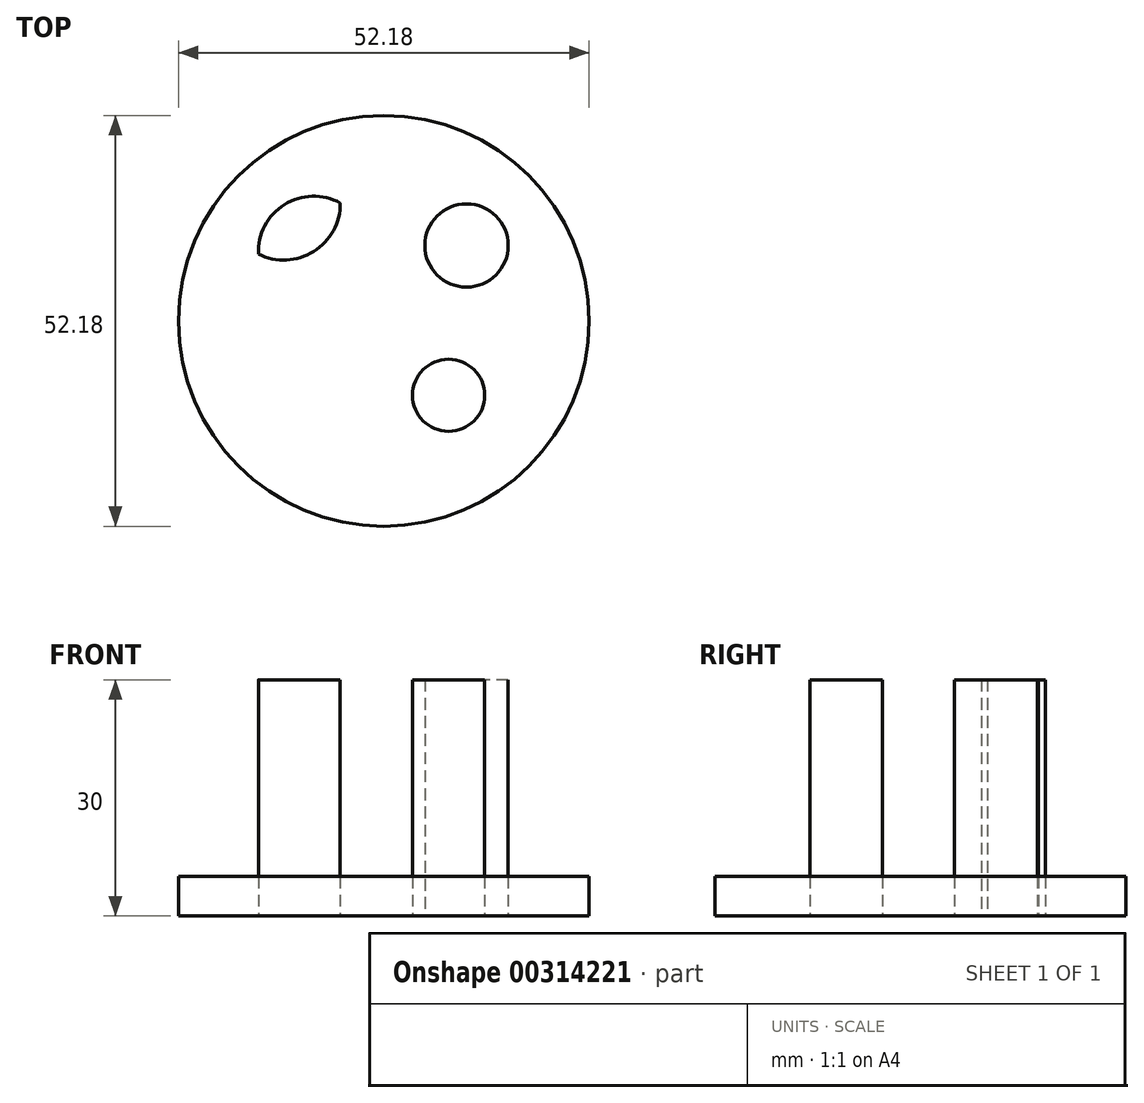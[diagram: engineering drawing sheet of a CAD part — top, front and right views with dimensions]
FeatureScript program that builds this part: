
annotation { "Feature Type Name" : "Feature", "Feature Type Description" : "" }
export const myFeature = defineFeature(function(context is Context, id is Id, definition is map)
    precondition{}
    {
        {
            var Q0;
            Q0=qCreatedBy(makeId("Top.planeOp"),FACE);
            var sketch = newSketch(context, id + "F0", { "sketchPlane" : qUnion([Q0])});
            skCircle(sketch, "E0", {"center": v(0, 0) * mm, "radius": 26.1 * mm});
            skCircle(sketch, "E1", {"center": v(10.52, 9.59) * mm, "radius": 5.29 * mm});
            skCircle(sketch, "E2", {"center": v(8.23, -9.44) * mm, "radius": 4.58 * mm});
            skCircle(sketch, "E3", {"center": v(-12.7, 14.92) * mm, "radius": 7.18 * mm});
            skCircle(sketch, "E4", {"center": v(-8.9, 8.83) * mm, "radius": 7.02 * mm});
            skSolve(sketch);
        }
        {
            var Q0;
            Q0=makeQuery(id+"F0.imprint","IMPRINT",FACE,{"disambiguationData":[TD([[makeQuery(id+"F0.imprint","IMPRINT",EDGE,{"derivedFrom":sQuery(id+"F0.wireOp",EDGE,"E1")}),1.0]])]});
            var Q1;
            Q1=makeQuery(id+"F0.imprint","IMPRINT",FACE,{"disambiguationData":[TD([[makeQuery(id+"F0.imprint","IMPRINT",EDGE,{"derivedFrom":sQuery(id+"F0.wireOp",EDGE,"E2")}),1.0]])]});
            var Q2;
            {var subQ0=sQuery(id+"F0.wireOp",EDGE,"E4");var subQ1=sQuery(id+"F0.wireOp",EDGE,"E3");var subQ2=makeQuery(id+"F0.imprint","INTERSECT",VERTEX,{"disambiguationData":[OD(0.0)],"derivedFrom":[subQ1,subQ0]});Q2=makeQuery(id+"F0.imprint","IMPRINT",FACE,{"disambiguationData":[TD([[makeQuery(id+"F0.imprint","IMPRINT",EDGE,{"disambiguationData":[TD([[subQ2,1.0]])],"derivedFrom":subQ1}),1.0]])]});}
            extrude(context, id + "F1", {"entities" : qUnion([Q0, Q1, Q2]), "depth" : 30 * mm});
        }
        {
            var Q0;
            Q0=makeQuery(id+"F0.imprint","IMPRINT",FACE,{"disambiguationData":[TD([[makeQuery(id+"F0.imprint","IMPRINT",EDGE,{"derivedFrom":sQuery(id+"F0.wireOp",EDGE,"E1")}),-1.0]])]});
            var Q1;
            Q1=makeQuery(id+"F0.imprint","IMPRINT",FACE,{"disambiguationData":[TD([[makeQuery(id+"F0.imprint","IMPRINT",EDGE,{"derivedFrom":sQuery(id+"F0.wireOp",EDGE,"E2")}),1.0]])]});
            var Q2;
            Q2=makeQuery(id+"F0.imprint","IMPRINT",FACE,{"disambiguationData":[TD([[makeQuery(id+"F0.imprint","IMPRINT",EDGE,{"derivedFrom":sQuery(id+"F0.wireOp",EDGE,"E1")}),1.0]])]});
            var Q3;
            {var subQ0=sQuery(id+"F0.wireOp",EDGE,"E4");var subQ1=sQuery(id+"F0.wireOp",EDGE,"E3");var subQ2=makeQuery(id+"F0.imprint","INTERSECT",VERTEX,{"disambiguationData":[OD(0.0)],"derivedFrom":[subQ1,subQ0]});Q3=makeQuery(id+"F0.imprint","IMPRINT",FACE,{"disambiguationData":[TD([[makeQuery(id+"F0.imprint","IMPRINT",EDGE,{"disambiguationData":[TD([[subQ2,1.0]])],"derivedFrom":subQ1}),-1.0]])]});}
            var Q4;
            {var subQ0=sQuery(id+"F0.wireOp",EDGE,"E4");var subQ1=sQuery(id+"F0.wireOp",EDGE,"E3");var subQ2=makeQuery(id+"F0.imprint","INTERSECT",VERTEX,{"disambiguationData":[OD(0.0)],"derivedFrom":[subQ1,subQ0]});Q4=makeQuery(id+"F0.imprint","IMPRINT",FACE,{"disambiguationData":[TD([[makeQuery(id+"F0.imprint","IMPRINT",EDGE,{"disambiguationData":[TD([[subQ2,1.0]])],"derivedFrom":subQ1}),1.0]])]});}
            var Q5;
            {var subQ0=sQuery(id+"F0.wireOp",EDGE,"E3");var subQ1=sQuery(id+"F0.wireOp",EDGE,"E0");var subQ2=makeQuery(id+"F0.imprint","INTERSECT",VERTEX,{"disambiguationData":[OD(0.0)],"derivedFrom":[subQ1,subQ0]});Q5=makeQuery(id+"F0.imprint","IMPRINT",FACE,{"disambiguationData":[TD([[makeQuery(id+"F0.imprint","IMPRINT",EDGE,{"disambiguationData":[TD([[subQ2,-1.0]])],"derivedFrom":subQ1}),1.0]])]});}
            extrude(context, id + "F2", {"entities" : qUnion([Q0, Q1, Q2, Q3, Q4, Q5]), "depth" : 5 * mm});
        }
    });
